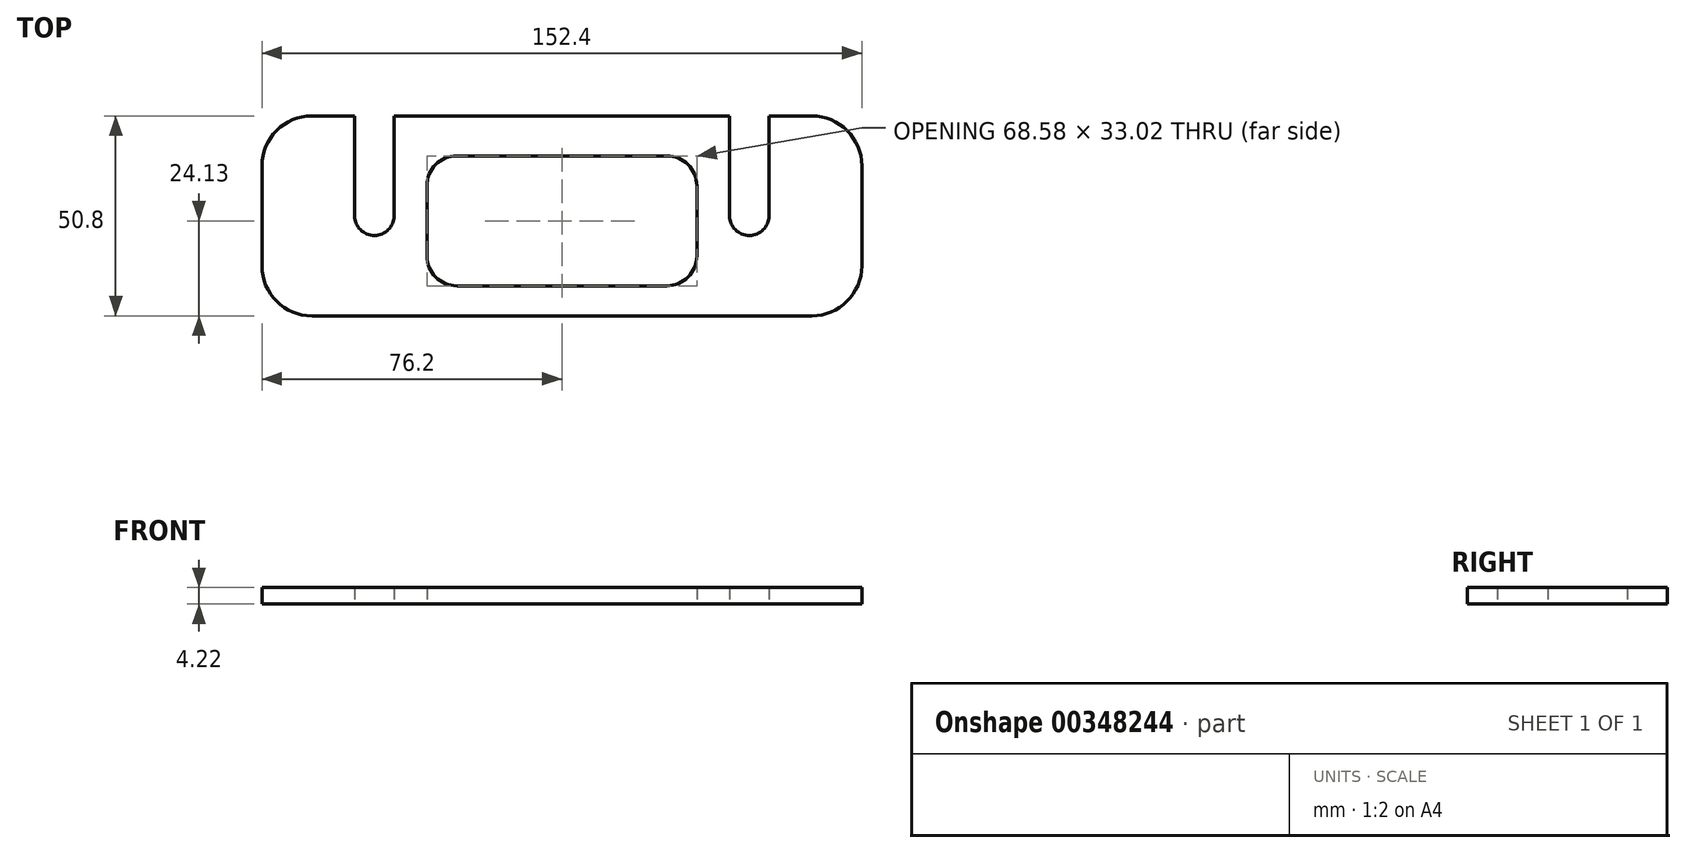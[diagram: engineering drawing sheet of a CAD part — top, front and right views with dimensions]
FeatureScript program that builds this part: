
annotation { "Feature Type Name" : "Feature", "Feature Type Description" : "" }
export const myFeature = defineFeature(function(context is Context, id is Id, definition is map)
    precondition{}
    {
        {
            var Q0;
            Q0=qCreatedBy(makeId("Top.planeOp"),FACE);
            var sketch = newSketch(context, id + "F0", { "sketchPlane" : qUnion([Q0])});
            skLineSegment(sketch, "E0.bottom", {"start": v(-139.7, 50.8) * mm, "end": v(-128.82, 50.8) * mm});
            skLineSegment(sketch, "E0.top", {"start": v(-139.7, 0) * mm, "end": v(-12.7, 0) * mm});
            skLineSegment(sketch, "E0.left", {"start": v(-152.4, 38.1) * mm, "end": v(-152.4, 12.7) * mm});
            skLineSegment(sketch, "E0.right", {"start": v(0, 38.1) * mm, "end": v(0, 12.7) * mm});
            skLineSegment(sketch, "E1", {"start": v(-76.2, 50.8) * mm, "end": v(-76.2, 0) * mm, "construction": true});
            skLineSegment(sketch, "E2.0", {"start": v(-123.83, 50.8) * mm, "end": v(-123.83, 0) * mm, "construction": true});
            skLineSegment(sketch, "E3.MirrorCS", {"start": v(-28.57, 50.8) * mm, "end": v(-28.57, 0) * mm, "construction": true});
            skLineSegment(sketch, "E4.0", {"start": v(-23.58, 50.8) * mm, "end": v(-23.58, 25.4) * mm});
            skLineSegment(sketch, "E5.0", {"start": v(-33.57, 50.8) * mm, "end": v(-33.57, 25.4) * mm});
            skLineSegment(sketch, "E6.MirrorCS", {"start": v(-118.83, 50.8) * mm, "end": v(-118.83, 25.4) * mm});
            skLineSegment(sketch, "E7.MirrorCS", {"start": v(-128.82, 50.8) * mm, "end": v(-128.82, 25.4) * mm});
            skArc(sketch, "E8", {"start": v(-128.82, 25.4) * mm, "mid": v(-123.83, 20.4) * mm, "end": v(-118.83, 25.4) * mm});
            skArc(sketch, "E9.MirrorCS", {"start": v(-23.58, 25.4) * mm, "mid": v(-28.58, 20.4) * mm, "end": v(-33.58, 25.4) * mm});
            skPoint(sketch, "E10.orphan", {"position": v(-118.83, 0) * mm});
            skPoint(sketch, "E11.orphan", {"position": v(-128.82, 0) * mm});
            skPoint(sketch, "E12.orphan", {"position": v(-33.57, 0) * mm});
            skPoint(sketch, "E13.orphan", {"position": v(-23.58, 0) * mm});
            skPoint(sketch, "E14.visualSharp", {"position": v(-152.4, 50.8) * mm});
            skArc(sketch, "E14.filletArc", {"start": v(-139.7, 50.8) * mm, "mid": v(-148.68, 47.08) * mm, "end": v(-152.4, 38.1) * mm});
            skPoint(sketch, "E15.visualSharp", {"position": v(-152.4, 0) * mm});
            skArc(sketch, "E15.filletArc", {"start": v(-152.4, 12.7) * mm, "mid": v(-148.68, 3.72) * mm, "end": v(-139.7, 0) * mm});
            skPoint(sketch, "E16.visualSharp", {"position": v(0, 50.8) * mm});
            skArc(sketch, "E16.filletArc", {"start": v(0, 38.1) * mm, "mid": v(-3.72, 47.08) * mm, "end": v(-12.7, 50.8) * mm});
            skPoint(sketch, "E17.visualSharp", {"position": v(0, 0) * mm});
            skArc(sketch, "E17.filletArc", {"start": v(-12.7, 0) * mm, "mid": v(-3.72, 3.72) * mm, "end": v(0, 12.7) * mm});
            skLineSegment(sketch, "E18.trimOffspring", {"start": v(-118.83, 50.8) * mm, "end": v(-33.57, 50.8) * mm});
            skLineSegment(sketch, "E19.trimOffspring", {"start": v(-23.58, 50.8) * mm, "end": v(-12.7, 50.8) * mm});
            skLineSegment(sketch, "E20.0", {"start": v(-102.87, 40.64) * mm, "end": v(-49.53, 40.64) * mm});
            skLineSegment(sketch, "E21.MirrorCS", {"start": v(-110.5, 15.24) * mm, "end": v(-110.5, 33.02) * mm});
            skLineSegment(sketch, "E22.trimOffspring", {"start": v(-102.87, 7.62) * mm, "end": v(-49.53, 7.62) * mm});
            skLineSegment(sketch, "E23", {"start": v(-41.9, 15.24) * mm, "end": v(-41.9, 33.02) * mm});
            skPoint(sketch, "E24.visualSharp", {"position": v(-110.5, 40.64) * mm});
            skArc(sketch, "E24.filletArc", {"start": v(-102.87, 40.64) * mm, "mid": v(-108.26, 38.4) * mm, "end": v(-110.5, 33.02) * mm});
            skPoint(sketch, "E25.visualSharp", {"position": v(-110.5, 7.62) * mm});
            skArc(sketch, "E25.filletArc", {"start": v(-110.5, 15.24) * mm, "mid": v(-108.26, 9.85) * mm, "end": v(-102.87, 7.62) * mm});
            skPoint(sketch, "E26.visualSharp", {"position": v(-41.9, 7.62) * mm});
            skArc(sketch, "E26.filletArc", {"start": v(-49.53, 7.62) * mm, "mid": v(-44.14, 9.85) * mm, "end": v(-41.9, 15.24) * mm});
            skPoint(sketch, "E27.visualSharp", {"position": v(-41.9, 40.64) * mm});
            skArc(sketch, "E27.filletArc", {"start": v(-41.9, 33.02) * mm, "mid": v(-44.14, 38.4) * mm, "end": v(-49.53, 40.64) * mm});
            skLineSegment(sketch, "E28", {"start": v(-118.83, 50.8) * mm, "end": v(-128.82, 50.8) * mm, "construction": true});
            skSolve(sketch);
        }
        {
            var Q0;
            Q0 = qSketchRegion(id + "F0", true);
            extrude(context, id + "F1", {"entities" : qUnion([Q0]), "depth" : 4.22 * mm});
        }
    });
